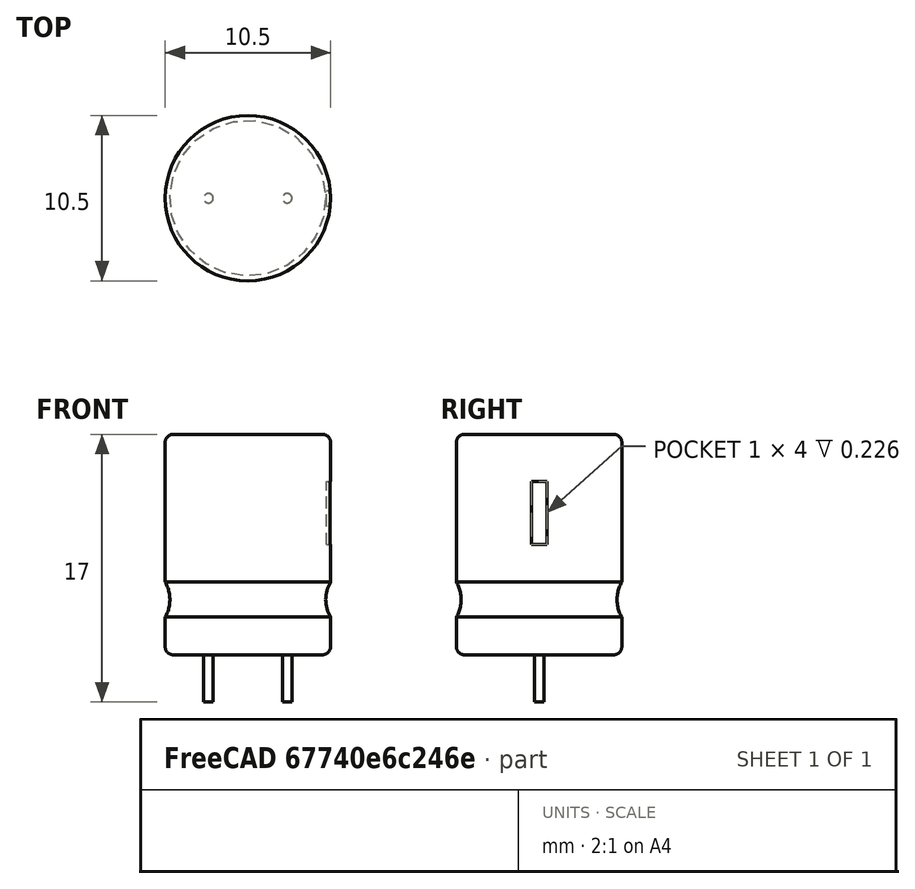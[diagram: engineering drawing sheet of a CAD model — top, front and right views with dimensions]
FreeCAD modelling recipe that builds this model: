
FCSTD DOCUMENT
Label: CAPPR500W60D1000H1250
License: CC-BY 3.0
LicenseURL: http://creativecommons.org/licenses/by/3.0/
objects: Part::Cylinder×3, Part::Cut×3, Part::Box×2, Part::Fuse×2, Part::Fillet×1, Part::Torus×1
note: 12 computed .brp shape members not serialized (recipe doc carries the construction recipe); baked Part::Feature solids carry a one-line shape summary decoded from their .brp

FEATURE [Part::Cylinder] Cylinder  label="Grundkoerper"
  Angle = 360
  Height = 14
  Radius = 5.25
FEATURE [Part::Cylinder] Cylinder001  label="Pin1+"
  Angle = 360
  Height = 3
  Placement = pos=(-2.5,0,-3) rot=(0,0,1;0rad)
  Radius = 0.3
FEATURE [Part::Cylinder] Cylinder002  label="Pin2-"
  Angle = 360
  Height = 3
  Placement = pos=(2.5,0,-3) rot=(0,0,1;0rad)
  Radius = 0.3
FEATURE [Part::Fillet] Fillet  label="Abgerundeter Grundkoerper"
  Base = -> Cylinder
  Edges = 2 edges r=0.5: [Edge1,Edge3]
FEATURE [Part::Torus] Torus  label="Ring"
  Angle1 = -180
  Angle2 = 180
  Angle3 = 360
  Placement = pos=(0,0,3.5) rot=(0,0,1;0rad)
  Radius1 = 7.15
  Radius2 = 2.2
FEATURE [Part::Cut] Cut  label="Beringter kondensator"
  Base = -> Fillet
  Tool = -> Torus
FEATURE [Part::Box] Box
  Height = 4
  Length = 1
  Placement = pos=(5,-0.5,7) rot=(0,0,1;0rad)
  Width = 1
FEATURE [Part::Box] Box001
  Height = 4
  Length = 1
  Placement = pos=(5,-0.5,15) rot=(0,0,1;0rad)
  Width = 1
FEATURE [Part::Cut] Cut001
  Base = -> Cut
  Tool = -> Box
FEATURE [Part::Cut] Cut002
  Base = -> Cut001
  Tool = -> Box001
FEATURE [Part::Fuse] Fusion
  Base = -> Cut002
  Tool = -> Cylinder001
FEATURE [Part::Fuse] Fusion001  label="CAPPR500W60D1000H1250"
  Base = -> Fusion
  Tool = -> Cylinder002
